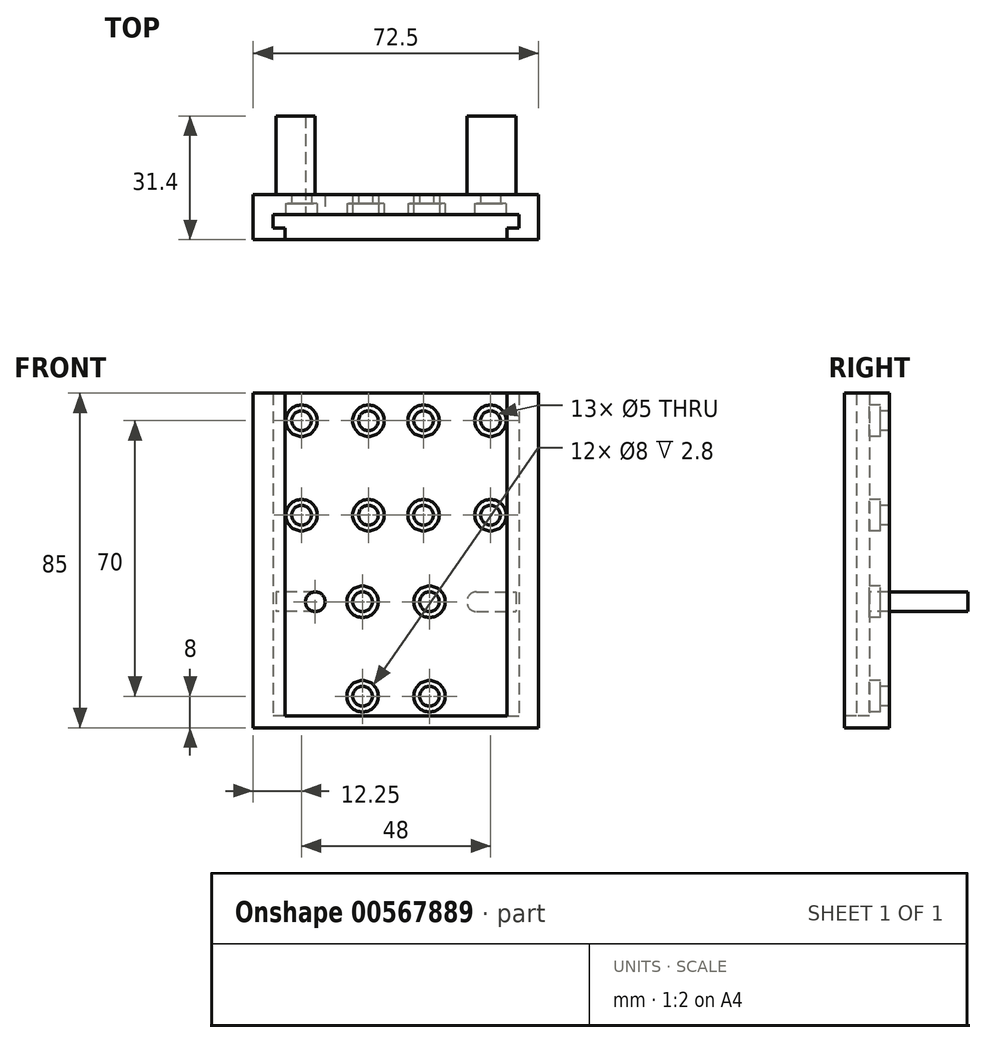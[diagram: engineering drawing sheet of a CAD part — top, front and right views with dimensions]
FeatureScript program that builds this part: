
annotation { "Feature Type Name" : "Feature", "Feature Type Description" : "" }
export const myFeature = defineFeature(function(context is Context, id is Id, definition is map)
    precondition{}
    {
        {
            var Q0;
            Q0=qCreatedBy(makeId("Front.planeOp"),FACE);
            var sketch = newSketch(context, id + "F0", { "sketchPlane" : qUnion([Q0])});
            skPoint(sketch, "E0", {"position": v(-8.5, -10.5) * mm});
            skPoint(sketch, "E1", {"position": v(8.5, -10.5) * mm});
            skPoint(sketch, "E2", {"position": v(-8.5, -34.5) * mm});
            skPoint(sketch, "E3", {"position": v(8.5, -34.5) * mm});
            skLineSegment(sketch, "E4.bottom", {"start": v(-36.25, 42.5) * mm, "end": v(36.25, 42.5) * mm});
            skLineSegment(sketch, "E5", {"start": v(0, -60.38) * mm, "end": v(0, 61.24) * mm, "construction": true});
            skPoint(sketch, "E6", {"position": v(0, 42.5) * mm});
            skLineSegment(sketch, "E7", {"start": v(36.25, 42.5) * mm, "end": v(36.25, -42.5) * mm});
            skLineSegment(sketch, "E8", {"start": v(36.25, -42.5) * mm, "end": v(-36.25, -42.5) * mm});
            skLineSegment(sketch, "E9", {"start": v(-36.25, -42.5) * mm, "end": v(-36.25, 42.5) * mm});
            skLineSegment(sketch, "E10", {"start": v(-64.65, 0) * mm, "end": v(70.3, 0) * mm, "construction": true});
            skPoint(sketch, "E11", {"position": v(-24, 35.5) * mm});
            skPoint(sketch, "E12", {"position": v(-7, 35.5) * mm});
            skPoint(sketch, "E13", {"position": v(-24, 11.5) * mm});
            skPoint(sketch, "E14", {"position": v(-7, 11.5) * mm});
            skPoint(sketch, "E15.MirrorP", {"position": v(24, 11.5) * mm});
            skPoint(sketch, "E16.MirrorP", {"position": v(7, 35.5) * mm});
            skPoint(sketch, "E17.MirrorP", {"position": v(24, 35.5) * mm});
            skPoint(sketch, "E18.MirrorP", {"position": v(7, 11.5) * mm});
            skCircle(sketch, "E19", {"center": v(20.5, -10.5) * mm, "radius": 2.5 * mm});
            skLineSegment(sketch, "E20", {"start": v(20.5, -8) * mm, "end": v(30.5, -8) * mm});
            skLineSegment(sketch, "E21", {"start": v(20.5, -13) * mm, "end": v(30.5, -13) * mm});
            skLineSegment(sketch, "E22.MirrorCS", {"start": v(-20.5, -8) * mm, "end": v(-30.5, -8) * mm});
            skLineSegment(sketch, "E23.MirrorCS", {"start": v(-20.5, -13) * mm, "end": v(-30.5, -13) * mm});
            skCircle(sketch, "E24.MirrorC", {"center": v(-20.5, -10.5) * mm, "radius": 2.5 * mm});
            skLineSegment(sketch, "E25", {"start": v(-30.5, -8) * mm, "end": v(-30.5, -13) * mm});
            skLineSegment(sketch, "E26", {"start": v(30.5, -8) * mm, "end": v(30.5, -13) * mm});
            skSolve(sketch);
        }
        {
            var Q0;
            Q0=makeQuery(id+"F0.imprint","IMPRINT",FACE,{"disambiguationData":[TD([[makeQuery(id+"F0.imprint","IMPRINT",EDGE,{"derivedFrom":sQuery(id+"F0.wireOp",EDGE,"E4.bottom")}),-1.0]])]});
            extrude(context, id + "F1", {"entities" : qUnion([Q0]), "flatOperationType" : FlatOperationType.REMOVE, "oppositeDirection" : true, "depth" : 5 * mm, "offsetDistance" : 25 * mm, "domain" : OperationDomain.MODEL});
        }
        {
            var Q0;
            Q0=sQuery(id+"F0.wireOp",VERTEX,"E11");
            var Q1;
            Q1=sQuery(id+"F0.wireOp",VERTEX,"E12");
            var Q2;
            Q2=sQuery(id+"F0.wireOp",VERTEX,"E13");
            var Q3;
            Q3=sQuery(id+"F0.wireOp",VERTEX,"E14");
            var Q4;
            Q4=sQuery(id+"F0.wireOp",VERTEX,"E16.MirrorP");
            var Q5;
            Q5=sQuery(id+"F0.wireOp",VERTEX,"E18.MirrorP");
            var Q6;
            Q6=sQuery(id+"F0.wireOp",VERTEX,"E17.MirrorP");
            var Q7;
            Q7=sQuery(id+"F0.wireOp",VERTEX,"E15.MirrorP");
            var Q8;
            Q8=sQuery(id+"F0.wireOp",VERTEX,"E0");
            var Q9;
            Q9=sQuery(id+"F0.wireOp",VERTEX,"E1");
            var Q10;
            Q10=sQuery(id+"F0.wireOp",VERTEX,"E2");
            var Q11;
            Q11=sQuery(id+"F0.wireOp",VERTEX,"E3");
            var Q12;
            Q12=makeQuery(id+"F1.opExtrude","SWEPT_BODY",BODY,{"disambiguationData":[OSD([sQuery(id+"F0.wireOp",EDGE,"E4.bottom"),sQuery(id+"F0.wireOp",EDGE,"E7"),sQuery(id+"F0.wireOp",EDGE,"E8"),sQuery(id+"F0.wireOp",EDGE,"E9")])]});
            hole(context, id + "F2", {"style" : HoleStyle.C_BORE, "endStyle" : HoleEndStyle.THROUGH, "holeDiameter" : 5 * mm, "cBoreDiameter" : 8 * mm, "cBoreDepth" : 2.8 * mm, "isTappedThrough" : true, "tappedDepth" : 12 * mm, "tapClearance" : 3, "locations" : qUnion([Q0, Q1, Q2, Q3, Q4, Q5, Q6, Q7, Q8, Q9, Q10, Q11]), "scope" : qUnion([Q12]), "majorDiameter" : 5 * mm});
        }
        {
            var Q0;
            Q0=makeQuery(id+"F1.opExtrude","SWEPT_FACE",FACE,{"disambiguationData":[OSD([sQuery(id+"F0.wireOp",EDGE,"E8")])]});
            var sketch = newSketch(context, id + "F3", { "sketchPlane" : qUnion([Q0])});
            skLineSegment(sketch, "E27", {"start": v(36.25, 6.4) * mm, "end": v(36.25, 0) * mm});
            skLineSegment(sketch, "E28", {"start": v(36.25, 6.4) * mm, "end": v(28.25, 6.4) * mm});
            skLineSegment(sketch, "E29", {"start": v(28.25, 3.4) * mm, "end": v(28.25, 6.4) * mm});
            skLineSegment(sketch, "E30", {"start": v(28.25, 3.4) * mm, "end": v(31.25, 3.4) * mm});
            skLineSegment(sketch, "E31", {"start": v(31.25, 0) * mm, "end": v(31.25, 3.4) * mm});
            skLineSegment(sketch, "E32", {"start": v(0, 11.66) * mm, "end": v(0, 0) * mm, "construction": true});
            skPoint(sketch, "E32.endSnap0", {"position": v(0, 0) * mm});
            skLineSegment(sketch, "E33.MirrorCS", {"start": v(-31.25, 0) * mm, "end": v(-31.25, 3.4) * mm});
            skLineSegment(sketch, "E34.MirrorCS", {"start": v(-28.25, 3.4) * mm, "end": v(-31.25, 3.4) * mm});
            skLineSegment(sketch, "E35.MirrorCS", {"start": v(-28.25, 3.4) * mm, "end": v(-28.25, 6.4) * mm});
            skLineSegment(sketch, "E36.MirrorCS", {"start": v(-36.25, 6.4) * mm, "end": v(-28.25, 6.4) * mm});
            skLineSegment(sketch, "E37.MirrorCS", {"start": v(-36.25, 6.4) * mm, "end": v(-36.25, 0) * mm});
            skLineSegment(sketch, "E38", {"start": v(-28.25, 6.4) * mm, "end": v(28.25, 6.4) * mm});
            skSolve(sketch);
        }
        {
            var Q0;
            {var subQ0=sQuery(id+"F3.wireOp",EDGE,"E33.MirrorCS");Q0=makeQuery(id+"F3.imprint","IMPRINT",FACE,{"disambiguationData":[TD([[makeQuery(id+"F3.imprint","IMPRINT",EDGE,{"derivedFrom":subQ0}),1.0]])]});}
            var Q1;
            {var subQ0=sQuery(id+"F3.wireOp",EDGE,"E27");Q1=makeQuery(id+"F3.imprint","IMPRINT",FACE,{"disambiguationData":[TD([[makeQuery(id+"F3.imprint","IMPRINT",EDGE,{"derivedFrom":subQ0}),-1.0]])]});}
            extrude(context, id + "F4", {"entities" : qUnion([Q0, Q1]), "operationType" : NewBodyOperationType.ADD, "flatOperationType" : FlatOperationType.REMOVE, "oppositeDirection" : true, "depth" : 85 * mm, "offsetDistance" : 25 * mm, "domain" : OperationDomain.MODEL});
        }
        {
            var Q0;
            Q0=makeQuery(id+"F3.imprint","IMPRINT",FACE,{"disambiguationData":[TD([[makeQuery(id+"F3.imprint","IMPRINT",EDGE,{"derivedFrom":sQuery(id+"F3.wireOp",EDGE,"E29")}),1.0]])]});
            extrude(context, id + "F5", {"entities" : qUnion([Q0]), "operationType" : NewBodyOperationType.ADD, "flatOperationType" : FlatOperationType.REMOVE, "oppositeDirection" : true, "depth" : 3 * mm, "offsetDistance" : 25 * mm, "domain" : OperationDomain.MODEL});
        }
        {
            var Q0;
            {var subQ0=sQuery(id+"F0.wireOp",EDGE,"cd5f94b3-c83e-41d8-b61d-e09703be21b9");var subQ1=makeQuery(id+"F0.imprint","INTERSECT",VERTEX,{"derivedFrom":[subQ0,sQuery(id+"F0.wireOp",EDGE,"E20")]});Q0=makeQuery(id+"F0.imprint","IMPRINT",FACE,{"disambiguationData":[TD([[makeQuery(id+"F0.imprint","IMPRINT",EDGE,{"disambiguationData":[TD([[subQ1,-1.0]])],"derivedFrom":subQ0}),1.0]])]});}
            var Q1;
            {var subQ0=sQuery(id+"F0.wireOp",EDGE,"E19");var subQ1=makeQuery(id+"F0.imprint","INTERSECT",VERTEX,{"derivedFrom":[subQ0,sQuery(id+"F0.wireOp",EDGE,"E20")]});Q1=makeQuery(id+"F0.imprint","IMPRINT",FACE,{"disambiguationData":[TD([[makeQuery(id+"F0.imprint","IMPRINT",EDGE,{"disambiguationData":[TD([[subQ1,-1.0]])],"derivedFrom":subQ0}),1.0]])]});}
            var Q2;
            {var subQ0=sQuery(id+"F0.wireOp",EDGE,"E20");Q2=makeQuery(id+"F0.imprint","IMPRINT",FACE,{"disambiguationData":[TD([[makeQuery(id+"F0.imprint","IMPRINT",EDGE,{"derivedFrom":subQ0}),-1.0]])]});}
            var Q3;
            {var subQ0=sQuery(id+"F0.wireOp",EDGE,"E24.MirrorC");var subQ1=makeQuery(id+"F0.imprint","INTERSECT",VERTEX,{"derivedFrom":[sQuery(id+"F0.wireOp",EDGE,"E22.MirrorCS"),subQ0]});Q3=makeQuery(id+"F0.imprint","IMPRINT",FACE,{"disambiguationData":[TD([[makeQuery(id+"F0.imprint","IMPRINT",EDGE,{"disambiguationData":[TD([[subQ1,-1.0]])],"derivedFrom":subQ0}),-1.0]])]});}
            var Q4;
            {var subQ0=sQuery(id+"F0.wireOp",EDGE,"E22.MirrorCS");Q4=makeQuery(id+"F0.imprint","IMPRINT",FACE,{"disambiguationData":[TD([[makeQuery(id+"F0.imprint","IMPRINT",EDGE,{"derivedFrom":subQ0}),1.0]])]});}
            var Q5;
            {var subQ0=sQuery(id+"F0.wireOp",EDGE,"f1632cb7-14f9-40b8-a853-77eba36881490.MirrorC");var subQ1=makeQuery(id+"F0.imprint","INTERSECT",VERTEX,{"derivedFrom":[subQ0,sQuery(id+"F0.wireOp",EDGE,"E22.MirrorCS")]});Q5=makeQuery(id+"F0.imprint","IMPRINT",FACE,{"disambiguationData":[TD([[makeQuery(id+"F0.imprint","IMPRINT",EDGE,{"disambiguationData":[TD([[subQ1,-1.0]])],"derivedFrom":subQ0}),-1.0]])]});}
            extrude(context, id + "F6", {"entities" : qUnion([Q0, Q1, Q2, Q3, Q4, Q5]), "operationType" : NewBodyOperationType.ADD, "oppositeDirection" : true, "depth" : 25 * mm, "offsetDistance" : 25 * mm});
        }
    });
